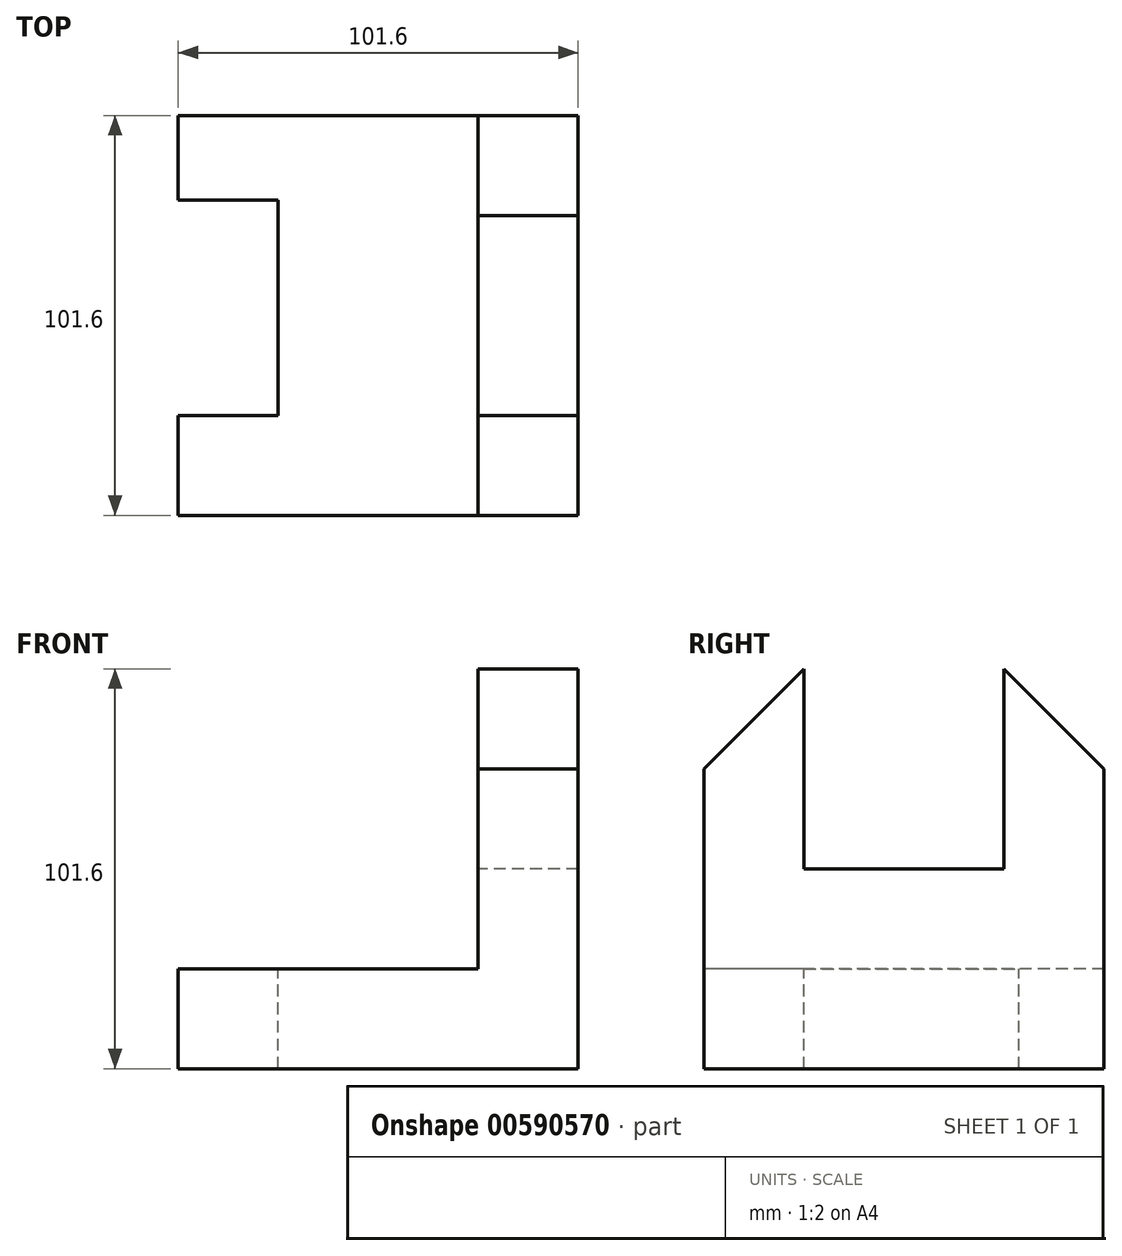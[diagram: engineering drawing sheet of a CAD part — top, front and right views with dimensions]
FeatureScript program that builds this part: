
annotation { "Feature Type Name" : "Feature", "Feature Type Description" : "" }
export const myFeature = defineFeature(function(context is Context, id is Id, definition is map)
    precondition{}
    {
        {
            var Q0;
            Q0=qCreatedBy(makeId("Top.planeOp"),FACE);
            var sketch = newSketch(context, id + "F0", { "sketchPlane" : qUnion([Q0])});
            skLineSegment(sketch, "E0.bottom", {"start": v(0, 0) * mm, "end": v(-101.6, 0) * mm});
            skLineSegment(sketch, "E0.top", {"start": v(0, -101.6) * mm, "end": v(-101.6, -101.6) * mm});
            skLineSegment(sketch, "E0.left", {"start": v(0, 0) * mm, "end": v(0, -101.6) * mm});
            skLineSegment(sketch, "E0.right", {"start": v(-101.6, 0) * mm, "end": v(-101.6, -101.6) * mm});
            skSolve(sketch);
        }
        {
            var Q0;
            Q0=makeQuery(id+"F0.imprint","IMPRINT",FACE,{"disambiguationData":[TD([[makeQuery(id+"F0.imprint","IMPRINT",EDGE,{"derivedFrom":sQuery(id+"F0.wireOp",EDGE,"E0.bottom")}),1.0]])]});
            extrude(context, id + "F1", {"entities" : qUnion([Q0]), "depth" : 101.6 * mm, "offsetDistance" : 25.4 * mm});
        }
        {
            var Q0;
            Q0=makeQuery(id+"F1.opExtrude","SWEPT_FACE",FACE,{"disambiguationData":[OSD([sQuery(id+"F0.wireOp",EDGE,"E0.top")])]});
            var sketch = newSketch(context, id + "F2", { "sketchPlane" : qUnion([Q0])});
            skLineSegment(sketch, "E1.bottom", {"start": v(-101.6, 101.6) * mm, "end": v(-25.4, 101.6) * mm});
            skLineSegment(sketch, "E1.top", {"start": v(-101.6, 25.4) * mm, "end": v(-25.4, 25.4) * mm});
            skLineSegment(sketch, "E1.left", {"start": v(-101.6, 101.6) * mm, "end": v(-101.6, 25.4) * mm});
            skLineSegment(sketch, "E1.right", {"start": v(-25.4, 101.6) * mm, "end": v(-25.4, 25.4) * mm});
            skSolve(sketch);
        }
        {
            var Q0;
            Q0=makeQuery(id+"F2.imprint","IMPRINT",FACE,{"disambiguationData":[TD([[makeQuery(id+"F2.imprint","IMPRINT",EDGE,{"derivedFrom":sQuery(id+"F2.wireOp",EDGE,"E1.bottom")}),1.0]])]});
            extrude(context, id + "F3", {"entities" : qUnion([Q0]), "operationType" : NewBodyOperationType.REMOVE, "oppositeDirection" : true, "depth" : 168.9 * mm, "offsetDistance" : 25.4 * mm});
        }
        {
            var Q0;
            Q0=makeQuery(id+"F3.boolean.opBoolean","COPY",FACE,{"derivedFrom":makeQuery(id+"F3.opExtrude","SWEPT_FACE",FACE,{"disambiguationData":[OSD([sQuery(id+"F2.wireOp",EDGE,"E1.top")])]})});
            var sketch = newSketch(context, id + "F4", { "sketchPlane" : qUnion([Q0])});
            skLineSegment(sketch, "E2.bottom", {"start": v(-101.6, -101.6) * mm, "end": v(-76.2, -101.6) * mm});
            skLineSegment(sketch, "E2.top", {"start": v(-101.6, -76.2) * mm, "end": v(-76.2, -76.2) * mm});
            skLineSegment(sketch, "E2.left", {"start": v(-101.6, -101.6) * mm, "end": v(-101.6, -76.2) * mm});
            skLineSegment(sketch, "E2.right", {"start": v(-76.2, -101.6) * mm, "end": v(-76.2, -76.2) * mm});
            skLineSegment(sketch, "E3.top", {"start": v(-101.6, -21.56) * mm, "end": v(-76.2, -21.56) * mm});
            skLineSegment(sketch, "E3.left", {"start": v(-101.6, -76.2) * mm, "end": v(-101.6, -21.56) * mm});
            skLineSegment(sketch, "E3.right", {"start": v(-76.2, -76.2) * mm, "end": v(-76.2, -21.56) * mm});
            skSolve(sketch);
        }
        {
            var Q0;
            Q0=makeQuery(id+"F4.imprint","IMPRINT",FACE,{"disambiguationData":[TD([[makeQuery(id+"F4.imprint","IMPRINT",EDGE,{"derivedFrom":sQuery(id+"F4.wireOp",EDGE,"E2.top")}),1.0]])]});
            extrude(context, id + "F5", {"entities" : qUnion([Q0]), "operationType" : NewBodyOperationType.REMOVE, "oppositeDirection" : true, "depth" : 81.03 * mm, "offsetDistance" : 25.4 * mm});
        }
        {
            var Q0;
            Q0=makeQuery(id+"F3.boolean.opBoolean","COPY",FACE,{"derivedFrom":makeQuery(id+"F3.opExtrude","SWEPT_FACE",FACE,{"disambiguationData":[OSD([sQuery(id+"F2.wireOp",EDGE,"E1.right")])]})});
            var sketch = newSketch(context, id + "F6", { "sketchPlane" : qUnion([Q0])});
            skLineSegment(sketch, "E4.bottom", {"start": v(0, 101.6) * mm, "end": v(25.4, 101.6) * mm});
            skLineSegment(sketch, "E4.top", {"start": v(0, 76.2) * mm, "end": v(25.4, 76.2) * mm});
            skLineSegment(sketch, "E4.left", {"start": v(0, 101.6) * mm, "end": v(0, 76.2) * mm});
            skLineSegment(sketch, "E4.right", {"start": v(25.4, 101.6) * mm, "end": v(25.4, 76.2) * mm});
            skLineSegment(sketch, "E5.bottom", {"start": v(101.6, 101.6) * mm, "end": v(76.2, 101.6) * mm});
            skLineSegment(sketch, "E5.top", {"start": v(101.6, 76.2) * mm, "end": v(76.2, 76.2) * mm});
            skLineSegment(sketch, "E5.left", {"start": v(101.6, 101.6) * mm, "end": v(101.6, 76.2) * mm});
            skLineSegment(sketch, "E5.right", {"start": v(76.2, 101.6) * mm, "end": v(76.2, 76.2) * mm});
            skLineSegment(sketch, "E6.bottom", {"start": v(25.4, 101.6) * mm, "end": v(76.2, 101.6) * mm});
            skLineSegment(sketch, "E6.top", {"start": v(25.4, 50.8) * mm, "end": v(76.2, 50.8) * mm});
            skLineSegment(sketch, "E6.left", {"start": v(25.4, 101.6) * mm, "end": v(25.4, 50.8) * mm});
            skLineSegment(sketch, "E6.right", {"start": v(76.2, 101.6) * mm, "end": v(76.2, 50.8) * mm});
            skLineSegment(sketch, "E7", {"start": v(25.4, 101.6) * mm, "end": v(0, 76.2) * mm});
            skLineSegment(sketch, "E8", {"start": v(76.2, 101.6) * mm, "end": v(101.6, 76.2) * mm});
            skSolve(sketch);
        }
        {
            var Q0;
            Q0=makeQuery(id+"F6.imprint","IMPRINT",FACE,{"disambiguationData":[TD([[makeQuery(id+"F6.imprint","IMPRINT",EDGE,{"derivedFrom":sQuery(id+"F6.wireOp",EDGE,"E4.left")}),1.0]])]});
            var Q1;
            Q1=makeQuery(id+"F6.imprint","IMPRINT",FACE,{"disambiguationData":[TD([[makeQuery(id+"F6.imprint","IMPRINT",EDGE,{"derivedFrom":sQuery(id+"F6.wireOp",EDGE,"E5.left")}),-1.0]])]});
            var Q2;
            {var subQ3=sQuery(id+"F6.wireOp",EDGE,"E6.bottom");Q2=makeQuery(id+"F6.imprint","IMPRINT",FACE,{"disambiguationData":[TD([[makeQuery(id+"F6.imprint","IMPRINT",EDGE,{"derivedFrom":subQ3}),-1.0]])]});}
            extrude(context, id + "F7", {"entities" : qUnion([Q0, Q1, Q2]), "operationType" : NewBodyOperationType.REMOVE, "oppositeDirection" : true, "depth" : 51.56 * mm, "offsetDistance" : 25.4 * mm});
        }
    });
